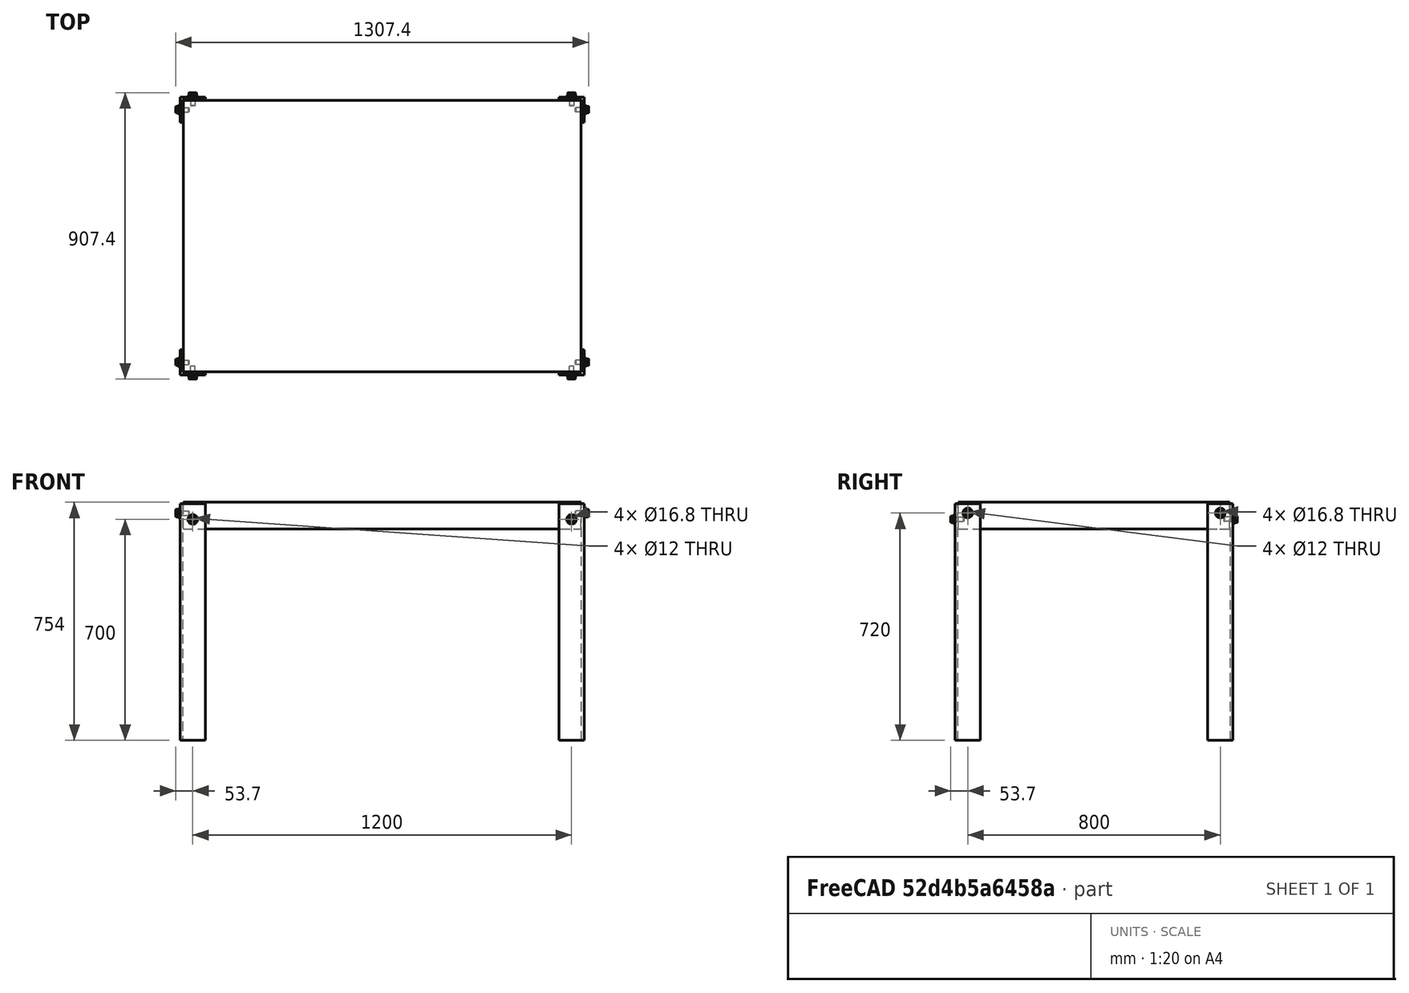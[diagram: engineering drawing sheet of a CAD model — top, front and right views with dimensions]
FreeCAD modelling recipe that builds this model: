
FCSTD DOCUMENT  (FreeCAD 0.18.3R)
Label: table
License: All rights reserved
LicenseURL: http://en.wikipedia.org/wiki/All_rights_reserved
objects: Part::Cut×12, Part::Box×9, Part::FeaturePython×8, Part::Cylinder×4
note: 33 computed .brp shape members not serialized (recipe doc carries the construction recipe); baked Part::Feature solids carry a one-line shape summary decoded from their .brp

FEATURE [Part::Box] Box  label="Cube"
  AttacherType = Attacher::AttachEngine3D
  Height = 750
  Length = 80
  Width = 80
FEATURE [Part::Box] Box001  label="Cube001"
  AttacherType = Attacher::AttachEngine3D
  Height = 750
  Length = 80
  Placement = pos=(8,8,0) rot=(0,0,1;0rad)
  Width = 80
FEATURE [Part::Cut] Cut
  Base = -> Box
  Tool = -> Box001
FEATURE [Part::Box] Box002  label="Cube002"
  AttacherType = Attacher::AttachEngine3D
  Height = 750
  Length = 80
  Placement = pos=(0,800,0) rot=(0,0,1;0rad)
  Width = 80
FEATURE [Part::Box] Box003  label="Cube003"
  AttacherType = Attacher::AttachEngine3D
  Height = 750
  Length = 80
  Placement = pos=(8,792,0) rot=(0,0,1;0rad)
  Width = 80
FEATURE [Part::Box] Box004  label="Cube004"
  AttacherType = Attacher::AttachEngine3D
  Height = 750
  Length = 80
  Placement = pos=(1200,0,0) rot=(0,0,1;0rad)
  Width = 80
FEATURE [Part::Box] Box005  label="Cube005"
  AttacherType = Attacher::AttachEngine3D
  Height = 750
  Length = 80
  Placement = pos=(1192,8,0) rot=(0,0,1;0rad)
  Width = 80
FEATURE [Part::Box] Box006  label="Cube006"
  AttacherType = Attacher::AttachEngine3D
  Height = 750
  Length = 80
  Placement = pos=(1200,800,0) rot=(0,0,1;0rad)
  Width = 80
FEATURE [Part::Box] Box007  label="Cube007"
  AttacherType = Attacher::AttachEngine3D
  Height = 750
  Length = 80
  Placement = pos=(1192,792,0) rot=(0,0,1;0rad)
  Width = 80
FEATURE [Part::Cut] Cut001
  Base = -> Box002
  Tool = -> Box003
FEATURE [Part::Cut] Cut002
  Base = -> Box004
  Tool = -> Box005
FEATURE [Part::Cut] Cut003
  Base = -> Box006
  Tool = -> Box007
FEATURE [Part::Cylinder] Cylinder
  Angle = 360
  AttacherType = Attacher::AttachEngine3D
  Height = 1300
  Placement = pos=(-10,40,720) rot=(0,1,0;1.5708rad)
  Radius = 6
FEATURE [Part::Cylinder] Cylinder001
  Angle = 360
  AttacherType = Attacher::AttachEngine3D
  Height = 1300
  Placement = pos=(-10,840,720) rot=(0,1,0;1.5708rad)
  Radius = 6
FEATURE [Part::Cylinder] Cylinder002
  Angle = 360
  AttacherType = Attacher::AttachEngine3D
  Height = 900
  Placement = pos=(40,-10,700) rot=(-1,0,0;1.5708rad)
  Radius = 6
FEATURE [Part::Cylinder] Cylinder003
  Angle = 360
  AttacherType = Attacher::AttachEngine3D
  Height = 900
  Placement = pos=(1240,-10,700) rot=(-1,0,0;1.5708rad)
  Radius = 6
FEATURE [Part::Cut] Cut004
  Base = -> Cut
  Tool = -> Cylinder
FEATURE [Part::Cut] Cut005
  Base = -> Cut002
  Tool = -> Cylinder
FEATURE [Part::Cut] Cut006  label="Metallic foot 1"
  Base = -> Cut004
  Tool = -> Cylinder002
FEATURE [Part::Cut] Cut007
  Base = -> Cut001
  Tool = -> Cylinder002
FEATURE [Part::Cut] Cut008  label="Metallic foot 2"
  Base = -> Cut007
  Tool = -> Cylinder001
FEATURE [Part::Cut] Cut009
  Base = -> Cut003
  Tool = -> Cylinder001
FEATURE [Part::Cut] Cut010  label="Metallic foot 3"
  Base = -> Cut005
  Tool = -> Cylinder003
FEATURE [Part::Cut] Cut011  label="Metallic foot 4"
  Base = -> Cut009
  Tool = -> Cylinder003
FEATURE [Part::Box] Box008  label="Tabletop"
  AttacherType = Attacher::AttachEngine3D
  Height = 84
  Length = 1260
  Placement = pos=(10,10,670) rot=(0,0,1;0rad)
  Width = 860
FEATURE [Part::FeaturePython] Screw  label="(M14)x30-Screw"  # Fasteners workbench fastener (typed FeaturePython)
  Placement = pos=(1282,40,720) rot=(0,1,0;1.5708rad)
  baseObject = -> Cut010 [Edge22]
  diameter = 6
  invert = false
  length = 0
  matchOuter = false
  offset = 2
  thread = false
  type = 2
FEATURE [Part::FeaturePython] Screw001  label="(M14)x30-Screw001"  # Fasteners workbench fastener (typed FeaturePython)
  Placement = pos=(1240,-2,700) rot=(1,0,0;1.5708rad)
  baseObject = -> Cut010 [Edge18]
  diameter = 6
  invert = true
  length = 0
  matchOuter = false
  offset = 2
  thread = false
  type = 2
FEATURE [Part::FeaturePython] Screw002  label="(M14)x30-Screw002"  # Fasteners workbench fastener (typed FeaturePython)
  Placement = pos=(1282,840,720) rot=(0,1,0;1.5708rad)
  baseObject = -> Cut011 [Edge20]
  diameter = 6
  invert = false
  length = 0
  matchOuter = false
  offset = 2
  thread = false
  type = 2
FEATURE [Part::FeaturePython] Screw003  label="(M14)x30-Screw003"  # Fasteners workbench fastener (typed FeaturePython)
  Placement = pos=(1240,882,700) rot=(-1,0,0;1.5708rad)
  baseObject = -> Cut011 [Edge12]
  diameter = 6
  invert = false
  length = 0
  matchOuter = false
  offset = 2
  thread = false
  type = 2
FEATURE [Part::FeaturePython] Screw004  label="(M14)x30-Screw004"  # Fasteners workbench fastener (typed FeaturePython)
  Placement = pos=(-2,40,720) rot=(0,-1,0;1.5708rad)
  baseObject = -> Cut006 [Edge5]
  diameter = 6
  invert = true
  length = 0
  matchOuter = false
  offset = 2
  thread = false
  type = 2
FEATURE [Part::FeaturePython] Screw005  label="(M14)x30-Screw005"  # Fasteners workbench fastener (typed FeaturePython)
  Placement = pos=(40,-2,700) rot=(1,0,0;1.5708rad)
  baseObject = -> Cut006 [Edge9]
  diameter = 6
  invert = true
  length = 0
  matchOuter = false
  offset = 2
  thread = false
  type = 2
FEATURE [Part::FeaturePython] Screw006  label="(M14)x30-Screw006"  # Fasteners workbench fastener (typed FeaturePython)
  Placement = pos=(-2,840,720) rot=(0,-1,0;1.5708rad)
  baseObject = -> Cut008 [Edge5]
  diameter = 6
  invert = true
  length = 0
  matchOuter = false
  offset = 2
  thread = false
  type = 2
FEATURE [Part::FeaturePython] Screw007  label="(M14)x30-Screw007"  # Fasteners workbench fastener (typed FeaturePython)
  Placement = pos=(40,882,700) rot=(-1,0,0;1.5708rad)
  baseObject = -> Cut008 [Edge18]
  diameter = 6
  invert = false
  length = 0
  matchOuter = false
  offset = 2
  thread = false
  type = 2
